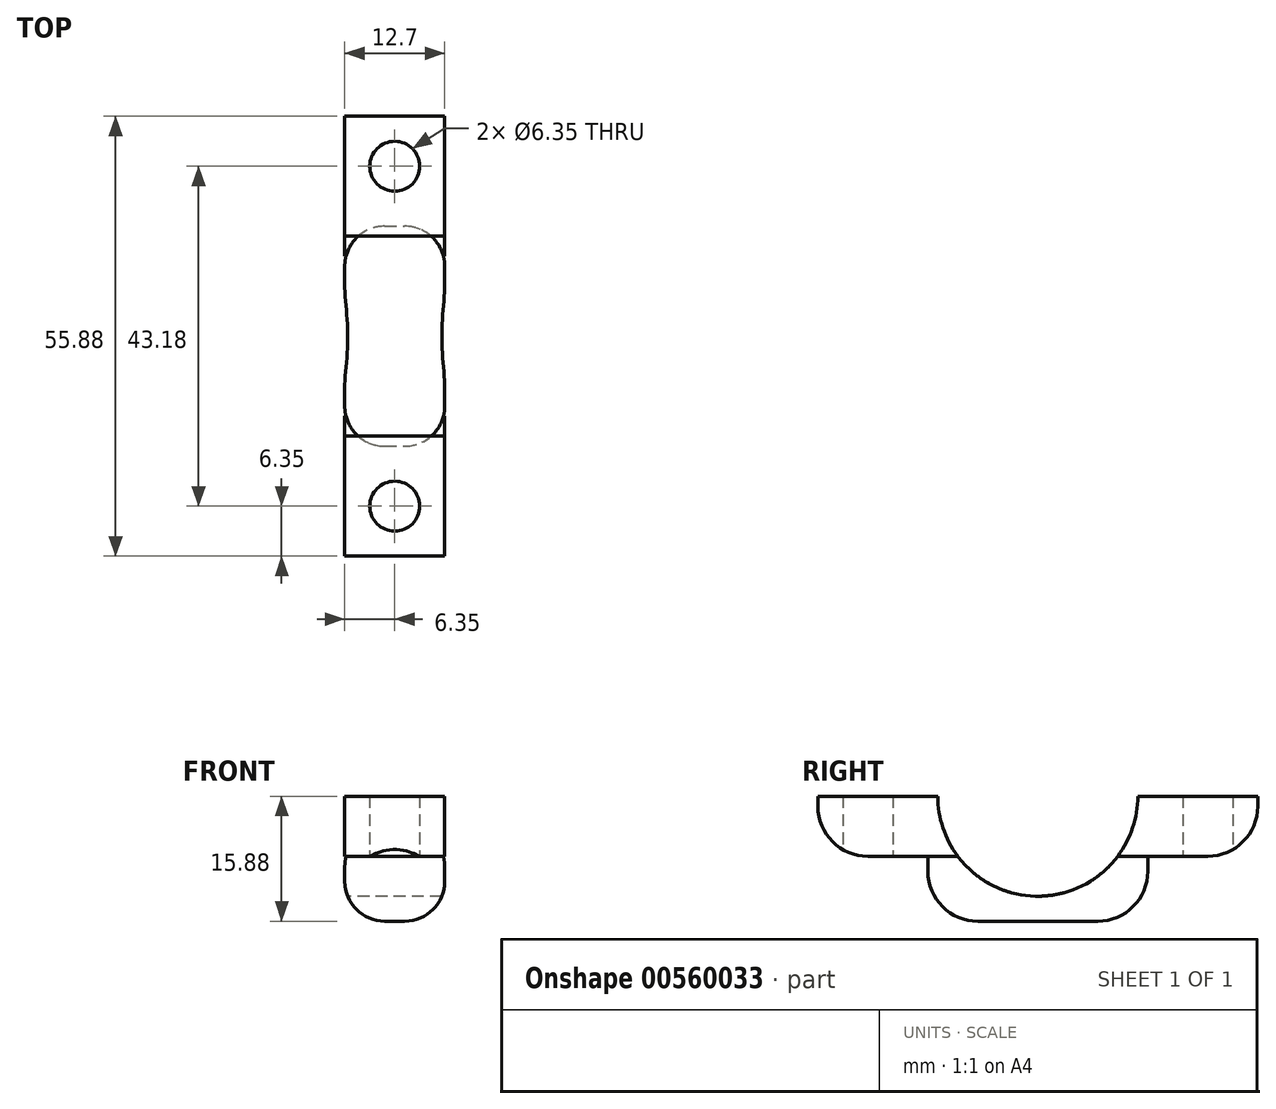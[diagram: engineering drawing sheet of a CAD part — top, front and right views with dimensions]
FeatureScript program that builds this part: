
annotation { "Feature Type Name" : "Feature", "Feature Type Description" : "" }
export const myFeature = defineFeature(function(context is Context, id is Id, definition is map)
    precondition{}
    {
        {
            var Q0;
            Q0=qCreatedBy(makeId("Front.planeOp"),FACE);
            var sketch = newSketch(context, id + "F0", { "sketchPlane" : qUnion([Q0])});
            skLineSegment(sketch, "E0", {"start": v(-12.7, 9.53) * mm, "end": v(-12.7, 25.4) * mm});
            skLineSegment(sketch, "E1", {"start": v(-12.7, 12.7) * mm, "end": v(-25.4, 12.7) * mm});
            skLineSegment(sketch, "E2", {"start": v(-25.4, 12.7) * mm, "end": v(-25.4, 25.4) * mm});
            skLineSegment(sketch, "E3", {"start": v(-25.4, 25.4) * mm, "end": v(-12.7, 25.4) * mm});
            skLineSegment(sketch, "E4", {"start": v(-25.4, 12.7) * mm, "end": v(-25.4, 9.53) * mm});
            skLineSegment(sketch, "E5", {"start": v(-25.4, 9.53) * mm, "end": v(-12.7, 9.53) * mm});
            skSolve(sketch);
        }
        {
            var Q0;
            Q0=qSketchRegion(id+"F0",true);
            extrude(context, id + "F1", {"entities" : qUnion([Q0]), "depth" : 27.94 * mm, "offsetDistance" : 25.4 * mm});
        }
        {
            var Q0;
            {var subQ0=sQuery(id+"F0.wireOp",EDGE,"VcH2IKVM-ps6W-ZrxU-62aj-0M5615qhgqus");var subQ1=sQuery(id+"F0.wireOp",EDGE,"E3");var subQ2=sQuery(id+"F0.wireOp",EDGE,"E2");Q0=makeQuery(id+"FD0ceM8fNLLehTe_1.boolean.opBoolean","SPLIT",FACE,{"disambiguationData":[TD([makeQuery(id+"F1.opExtrude","CAP_FACE",FACE,{"disambiguationData":[OSD([sQuery(id+"F0.wireOp",EDGE,"xeTE2oLe-OO5J-BHiE-ocNM-LQFFNbwLxTKm"),subQ2,subQ1,subQ0,sQuery(id+"F0.wireOp",EDGE,"H58Lk7TK-6iQ2-5jjx-BXkw-zgiEKpR37TL3"),sQuery(id+"F0.wireOp",EDGE,"ePR6JIEe-MF6X-ynQJ-Nzjn-kP2pOMX6ajSc")])],"isStart":false})])],"derivedFrom":makeQuery(id+"F1.opExtrude","SWEPT_FACE",FACE,{"disambiguationData":[OSD([subQ1])]})});}
            var sketch = newSketch(context, id + "F2", { "sketchPlane" : qUnion([Q0])});
            skLineSegment(sketch, "E6", {"start": v(-25.4, -27.94) * mm, "end": v(-25.4, -38.87) * mm});
            skLineSegment(sketch, "E7", {"start": v(-25.4, -38.87) * mm, "end": v(-12.7, -38.87) * mm});
            skLineSegment(sketch, "E8", {"start": v(-12.7, -38.87) * mm, "end": v(-12.7, -27.94) * mm});
            skLineSegment(sketch, "E9", {"start": v(-12.7, -27.94) * mm, "end": v(-12.7, -41.91) * mm});
            skLineSegment(sketch, "E10", {"start": v(-12.7, -41.91) * mm, "end": v(-25.4, -41.91) * mm});
            skLineSegment(sketch, "E11", {"start": v(-25.4, -41.91) * mm, "end": v(-25.4, -27.94) * mm});
            skSolve(sketch);
        }
        {
            var Q0;
            {var subQ0=sQuery(id+"F2.wireOp",EDGE,"E6");Q0=makeQuery(id+"F2.imprint","IMPRINT",FACE,{"disambiguationData":[TD([[makeQuery(id+"F2.imprint","IMPRINT",EDGE,{"derivedFrom":subQ0}),1.0]])]});}
            var Q1;
            {var subQ0=sQuery(id+"F2.wireOp",EDGE,"E9");Q1=makeQuery(id+"F2.imprint","IMPRINT",FACE,{"disambiguationData":[TD([[makeQuery(id+"F2.imprint","IMPRINT",EDGE,{"derivedFrom":subQ0}),-1.0]])]});}
            extrude(context, id + "F3", {"entities" : qUnion([Q0, Q1]), "operationType" : NewBodyOperationType.ADD, "oppositeDirection" : true, "depth" : 7.62 * mm, "offsetDistance" : 25.4 * mm});
        }
        {
            var Q0;
            {var subQ0=sQuery(id+"F0.wireOp",EDGE,"VcH2IKVM-ps6W-ZrxU-62aj-0M5615qhgqus");var subQ1=sQuery(id+"F0.wireOp",EDGE,"E3");var subQ2=sQuery(id+"F0.wireOp",EDGE,"E2");Q0=makeQuery(id+"FD0ceM8fNLLehTe_1.boolean.opBoolean","SPLIT",FACE,{"disambiguationData":[TD([makeQuery(id+"F1.opExtrude","CAP_FACE",FACE,{"disambiguationData":[OSD([sQuery(id+"F0.wireOp",EDGE,"xeTE2oLe-OO5J-BHiE-ocNM-LQFFNbwLxTKm"),subQ2,subQ1,subQ0,sQuery(id+"F0.wireOp",EDGE,"H58Lk7TK-6iQ2-5jjx-BXkw-zgiEKpR37TL3"),sQuery(id+"F0.wireOp",EDGE,"ePR6JIEe-MF6X-ynQJ-Nzjn-kP2pOMX6ajSc")])],"isStart":true})])],"derivedFrom":makeQuery(id+"F1.opExtrude","SWEPT_FACE",FACE,{"disambiguationData":[OSD([subQ1])]})});}
            var sketch = newSketch(context, id + "F4", { "sketchPlane" : qUnion([Q0])});
            skLineSegment(sketch, "E12.bottom", {"start": v(-25.4, 0) * mm, "end": v(-12.7, 0) * mm});
            skLineSegment(sketch, "E12.top", {"start": v(-25.4, 13.97) * mm, "end": v(-12.7, 13.97) * mm});
            skLineSegment(sketch, "E12.left", {"start": v(-25.4, 0) * mm, "end": v(-25.4, 13.97) * mm});
            skLineSegment(sketch, "E12.right", {"start": v(-12.7, 0) * mm, "end": v(-12.7, 13.97) * mm});
            skLineSegment(sketch, "E13.bottom", {"start": v(-12.7, 0) * mm, "end": v(-25.4, 0) * mm});
            skLineSegment(sketch, "E13.top", {"start": v(-12.7, 13.97) * mm, "end": v(-25.4, 13.97) * mm});
            skSolve(sketch);
        }
        {
            var Q0;
            Q0=makeQuery(id+"F4.imprint","IMPRINT",FACE,{"disambiguationData":[TD([[makeQuery(id+"F4.imprint","IMPRINT",EDGE,{"derivedFrom":sQuery(id+"F4.wireOp",EDGE,"E12.bottom")}),1.0]])]});
            var Q1;
            Q1=makeQuery(id+"F4.imprint","IMPRINT",FACE,{"disambiguationData":[TD([[makeQuery(id+"F4.imprint","IMPRINT",EDGE,{"derivedFrom":sQuery(id+"F4.wireOp",EDGE,"E13.bottom")}),1.0]])]});
            extrude(context, id + "F5", {"entities" : qUnion([Q0, Q1]), "operationType" : NewBodyOperationType.ADD, "oppositeDirection" : true, "depth" : 7.62 * mm, "offsetDistance" : 25.4 * mm});
        }
        {
            var Q0;
            Q0=makeQuery(id+"F5.boolean.opBoolean","MERGE",FACE,{"derivedFrom":[makeQuery(id+"F3.boolean.opBoolean","MERGE",FACE,{"derivedFrom":[makeQuery(id+"F1.opExtrude","SWEPT_FACE",FACE,{"disambiguationData":[OSD([sQuery(id+"F0.wireOp",EDGE,"E2"),sQuery(id+"F0.wireOp",EDGE,"E4")])]}),makeQuery(id+"F3.opExtrude","SWEPT_FACE",FACE,{"disambiguationData":[OSD([sQuery(id+"F2.wireOp",EDGE,"E11")])]})]}),makeQuery(id+"F5.opExtrude","SWEPT_FACE",FACE,{"disambiguationData":[OSD([sQuery(id+"F4.wireOp",EDGE,"E12.left")])]})]});
            var sketch = newSketch(context, id + "F6", { "sketchPlane" : qUnion([Q0])});
            skCircle(sketch, "E14", {"center": v(13.97, 25.4) * mm, "radius": 12.7 * mm});
            skSolve(sketch);
        }
        {
            var Q0;
            {var subQ0=sQuery(id+"F6.wireOp",EDGE,"E14");var subQ1=makeQuery(id+"F5.boolean.opBoolean","MERGE",EDGE,{"derivedFrom":[makeQuery(id+"F3.boolean.opBoolean","MERGE",EDGE,{"derivedFrom":[makeQuery(id+"F1.opExtrude","SWEPT_EDGE",EDGE,{"disambiguationData":[OSD([sQuery(id+"F0.wireOp",EDGE,"E2"),sQuery(id+"F0.wireOp",EDGE,"E3")])]}),makeQuery(id+"F3.opExtrude","CAP_EDGE",EDGE,{"disambiguationData":[OSD([sQuery(id+"F2.wireOp",EDGE,"E11")])],"isStart":true})]}),makeQuery(id+"F5.opExtrude","CAP_EDGE",EDGE,{"disambiguationData":[OSD([sQuery(id+"F4.wireOp",EDGE,"E12.left")])],"isStart":true})]});var subQ2=makeQuery(id+"F6.imprint","INTERSECT",VERTEX,{"disambiguationData":[OD(0.0)],"derivedFrom":[subQ1,subQ0]});Q0=makeQuery(id+"F6.imprint","IMPRINT",FACE,{"disambiguationData":[TD([[makeQuery(id+"F6.imprint","IMPRINT",EDGE,{"disambiguationData":[TD([[subQ2,1.0]])],"derivedFrom":subQ0}),1.0]])]});}
            extrude(context, id + "F7", {"entities" : qUnion([Q0]), "operationType" : NewBodyOperationType.REMOVE, "oppositeDirection" : true, "depth" : 25.4 * mm, "offsetDistance" : 25.4 * mm});
        }
        {
            var Q0;
            Q0=makeQuery(id+"F3.opExtrude","CAP_FACE",FACE,{"disambiguationData":[OSD([sQuery(id+"F0.wireOp",EDGE,"E3"),sQuery(id+"F2.wireOp",EDGE,"E9"),sQuery(id+"F2.wireOp",EDGE,"E10"),sQuery(id+"F2.wireOp",EDGE,"E11")])],"isStart":false});
            var sketch = newSketch(context, id + "F8", { "sketchPlane" : qUnion([Q0])});
            skCircle(sketch, "E15", {"center": v(-19.05, 35.56) * mm, "radius": 3.18 * mm});
            skPoint(sketch, "E15.centerSnap1", {"position": v(-19.05, 41.91) * mm});
            skLineSegment(sketch, "E16", {"start": v(-19.05, 35.56) * mm, "end": v(-19.05, 41.91) * mm});
            skSolve(sketch);
        }
        {
            var Q0;
            Q0=makeQuery(id+"F5.opExtrude","CAP_FACE",FACE,{"disambiguationData":[OSD([sQuery(id+"F4.wireOp",EDGE,"E13.bottom"),sQuery(id+"F4.wireOp",EDGE,"E13.top"),sQuery(id+"F4.wireOp",EDGE,"E12.right"),sQuery(id+"F4.wireOp",EDGE,"E12.left")])],"isStart":false});
            var sketch = newSketch(context, id + "F9", { "sketchPlane" : qUnion([Q0])});
            skCircle(sketch, "E17", {"center": v(-19.05, -7.62) * mm, "radius": 3.18 * mm});
            skPoint(sketch, "E17.centerSnap0", {"position": v(-19.05, -13.97) * mm});
            skLineSegment(sketch, "E18", {"start": v(-19.05, -7.62) * mm, "end": v(-19.05, -13.97) * mm});
            skSolve(sketch);
        }
        {
            var Q0;
            Q0=makeQuery(id+"F8.imprint","IMPRINT",FACE,{"disambiguationData":[TD([[makeQuery(id+"F8.imprint","IMPRINT",EDGE,{"derivedFrom":sQuery(id+"F8.wireOp",EDGE,"E15")}),1.0]])]});
            var Q1;
            Q1=makeQuery(id+"F9.imprint","IMPRINT",FACE,{"disambiguationData":[TD([[makeQuery(id+"F9.imprint","IMPRINT",EDGE,{"derivedFrom":sQuery(id+"F9.wireOp",EDGE,"E17")}),1.0]])]});
            extrude(context, id + "F10", {"entities" : qUnion([Q0, Q1]), "operationType" : NewBodyOperationType.REMOVE, "oppositeDirection" : true, "depth" : 25.4 * mm, "offsetDistance" : 25.4 * mm});
        }
        {
            var Q0;
            Q0=makeQuery(id+"F3.opExtrude","CAP_EDGE",EDGE,{"disambiguationData":[OSD([sQuery(id+"F2.wireOp",EDGE,"E10")])],"isStart":false});
            var Q1;
            Q1=makeQuery(id+"F5.opExtrude","CAP_EDGE",EDGE,{"disambiguationData":[OSD([sQuery(id+"F4.wireOp",EDGE,"E13.top")])],"isStart":false});
            var Q2;
            Q2=makeQuery(id+"F5.opExtrude","CAP_EDGE",EDGE,{"disambiguationData":[OSD([sQuery(id+"F4.wireOp",EDGE,"E12.top")])],"isStart":false});
            fillet(context, id + "F11", {"entities" : qUnion([Q0, Q1, Q2]), "radius" : 6.35 * mm, "tangentPropagation" : true, "allowEdgeOverflow" : false});
        }
        {
            var Q0;
            Q0=makeQuery(id+"F1.opExtrude","CAP_EDGE",EDGE,{"disambiguationData":[OSD([sQuery(id+"F0.wireOp",EDGE,"E5")])],"isStart":true});
            fillet(context, id + "F12", {"entities" : qUnion([Q0]), "radius" : 6.35 * mm, "tangentPropagation" : true, "allowEdgeOverflow" : false});
        }
        {
            var Q0;
            Q0=makeQuery(id+"F1.opExtrude","CAP_EDGE",EDGE,{"disambiguationData":[OSD([sQuery(id+"F0.wireOp",EDGE,"E5")])],"isStart":false});
            fillet(context, id + "F13", {"entities" : qUnion([Q0]), "radius" : 6.35 * mm, "tangentPropagation" : true, "allowEdgeOverflow" : false});
        }
        {
            var Q0;
            Q0=makeQuery(id+"F1.opExtrude","SWEPT_EDGE",EDGE,{"disambiguationData":[OSD([sQuery(id+"F0.wireOp",EDGE,"E0"),sQuery(id+"F0.wireOp",EDGE,"E5")])]});
            var Q1;
            Q1=makeQuery(id+"F1.opExtrude","SWEPT_EDGE",EDGE,{"disambiguationData":[OSD([sQuery(id+"F0.wireOp",EDGE,"E4"),sQuery(id+"F0.wireOp",EDGE,"E5")])]});
            fillet(context, id + "F14", {"entities" : qUnion([Q0, Q1]), "radius" : 5.08 * mm, "tangentPropagation" : true, "allowEdgeOverflow" : false});
        }
    });
